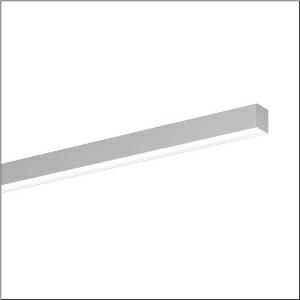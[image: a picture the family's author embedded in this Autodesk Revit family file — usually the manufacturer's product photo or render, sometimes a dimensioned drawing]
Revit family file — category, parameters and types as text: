
# Revit family: silica_r__21_51mx23da44sb_489f
name_source: partatom
category: Lighting Fixtures
units: mm (PartAtom-declared; Revit-internal decimal feet)

## family parameters
Cut with Voids When Loaded = No
Host = Face
Light Source = No
Part Type = Normal
Room Calculation Point = No
Round Connector Dimension = Use Diameter
Shared = No

## types (1)
- --- (1 x LED, 3280 lm, 22.4 W, 4000K)
    Apparent Load = 22 VA
    CIE Flux Codes = 78 96 99 100 100
    Color Rendering = 80
    Color Temperature = 4000K
    Default Elevation = 1800 mm
    Description = Silica® 21, office luminaire, primary optical cover: prismatic diffuser, of PMMA, CAT 2 (L<= 3000cd/m²), light emission: direct distribution, primary light characteristic: symmetric, installation type: surface-mounted, LED, rated luminous flux: 3.280lm, luminous efficacy: 146lm/W, light colour: 840, colour temperature: 4000K, control gear: DALI 2, with terminal, 3+2-pole, max. 2.5mm², mains connection: 220..240V, AC, 50/60Hz, rated input power: 22.4W, luminaire housing, of aluminium, metallic grey (RAL 9006), length: 1.204mm, width: 53mm, height: 53mm, protection rating (complete): IP20, insulation class (complete): insulation class I (protective earthing), certification: CE, permissible operating ambient temperature: 0..+35°C, standard: EN 50419, packaging unit: 1 piece
    Height = 53 mm
    Lamp = 1 x LED
    Lamp Light Flux = 3280 lm
    Lamp Power = 22.4 W
    Lamp count = 1
    Length = 1204 mm
    Luminous efficacy = 146 lm/W
    Manufacturer = Siteco
    ModVariant = No
    Model = 51MX23DA44SB
    Mounting Place = Ceiling
    Mounting Type = Surface mounted
    Number of Poles = 1
    OnlyDefault = Yes
    Power Factor = 1
    Product Name = Silica® 21
    Product group = office luminaire | ceiling mounted
    ProductGroupID = 303
    Protection Class = Protection class I
    Protection Degree = IP 20
    RLX_Detail_Level = 1
    RLX_Emergency_Light_Flux = 0 lm
    RLX_Emergency_Type = 0
    RLX_Emergency_Type_DB = No
    RlxData = <blob elided: 21241 chars, md5=39fcf5d9>
    Socket = socket
    Standby Power = 0 W
    System Light Flux = 3280 lm
    System Power = 22 W
    Type Comments = factory setting: luminous flux: 100 % | dim-lin: 254 | 323 mA
    Type Image = l_1335933.jpg
    URL = http://relux.com
    VarID = @adj_026993
    Voltage = 0 V
    Weight = 0.00 kg
    Width = 53 mm

## geometry (parser evidence)
native form markers: Blend x4, Sweep x11
no freeform markers — native parametric forms only
